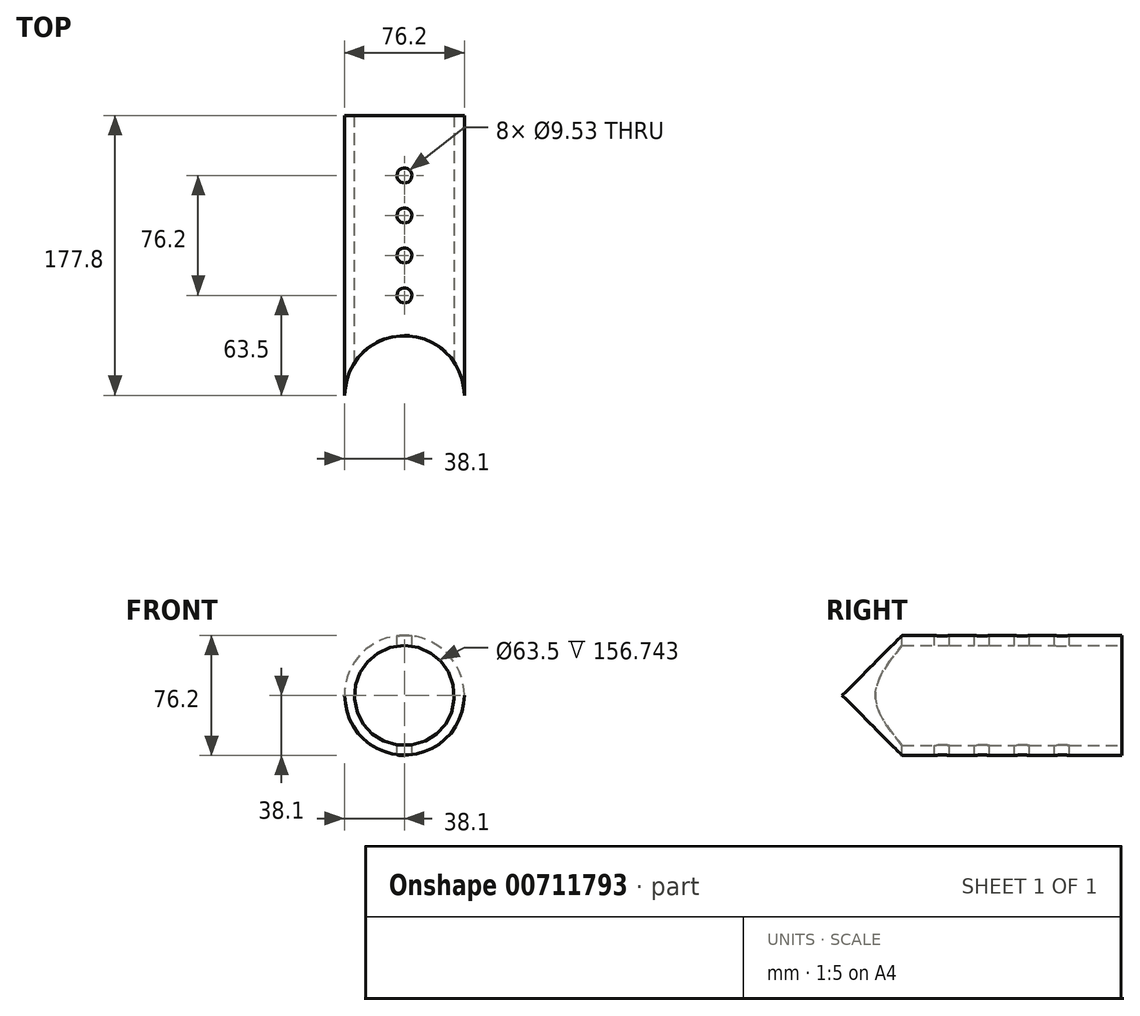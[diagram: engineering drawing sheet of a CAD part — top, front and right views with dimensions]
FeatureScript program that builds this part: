
annotation { "Feature Type Name" : "Feature", "Feature Type Description" : "" }
export const myFeature = defineFeature(function(context is Context, id is Id, definition is map)
    precondition{}
    {
        {
            var Q0;
            Q0=qCreatedBy(makeId("Front.planeOp"),FACE);
            var sketch = newSketch(context, id + "F0", { "sketchPlane" : qUnion([Q0])});
            skCircle(sketch, "E0", {"center": v(0, 0) * mm, "radius": 38.1 * mm});
            skCircle(sketch, "E1", {"center": v(0, 0) * mm, "radius": 31.75 * mm});
            skSolve(sketch);
        }
        {
            var Q0;
            Q0 = qSketchRegion(id + "F0", true);
            extrude(context, id + "F1", {"entities" : qUnion([Q0]), "endBound" : BoundingType.SYMMETRIC, "depth" : 177.8 * mm, "offsetDistance" : 25.4 * mm});
        }
        {
            var Q0;
            Q0=qCreatedBy(makeId("Top.planeOp"),FACE);
            var sketch = newSketch(context, id + "F2", { "sketchPlane" : qUnion([Q0])});
            skCircle(sketch, "E2", {"center": v(0, -88.9) * mm, "radius": 38.1 * mm});
            skSolve(sketch);
        }
        {
            var Q0;
            Q0=makeQuery(id+"F2.imprint","IMPRINT",FACE,{"disambiguationData":[TD([[makeQuery(id+"F2.imprint","IMPRINT",EDGE,{"derivedFrom":sQuery(id+"F2.wireOp",EDGE,"E2")}),1.0]])]});
            extrude(context, id + "F3", {"entities" : qUnion([Q0]), "operationType" : NewBodyOperationType.REMOVE, "endBound" : BoundingType.SYMMETRIC, "oppositeDirection" : true, "depth" : 76.2 * mm, "offsetDistance" : 25.4 * mm});
        }
        {
            var Q0;
            Q0=qCreatedBy(makeId("Top.planeOp"),FACE);
            var sketch = newSketch(context, id + "F4", { "sketchPlane" : qUnion([Q0])});
            skCircle(sketch, "E3", {"center": v(0, 50.8) * mm, "radius": 4.76 * mm});
            skCircle(sketch, "E4", {"center": v(0, 25.4) * mm, "radius": 4.76 * mm});
            skCircle(sketch, "E5", {"center": v(0, 0) * mm, "radius": 4.76 * mm});
            skCircle(sketch, "E6", {"center": v(0, -25.4) * mm, "radius": 4.76 * mm});
            skSolve(sketch);
        }
        {
            var Q0;
            Q0 = qSketchRegion(id + "F4", true);
            extrude(context, id + "F5", {"entities" : qUnion([Q0]), "operationType" : NewBodyOperationType.REMOVE, "endBound" : BoundingType.SYMMETRIC, "oppositeDirection" : true, "depth" : 76.2 * mm, "offsetDistance" : 25.4 * mm});
        }
    });
